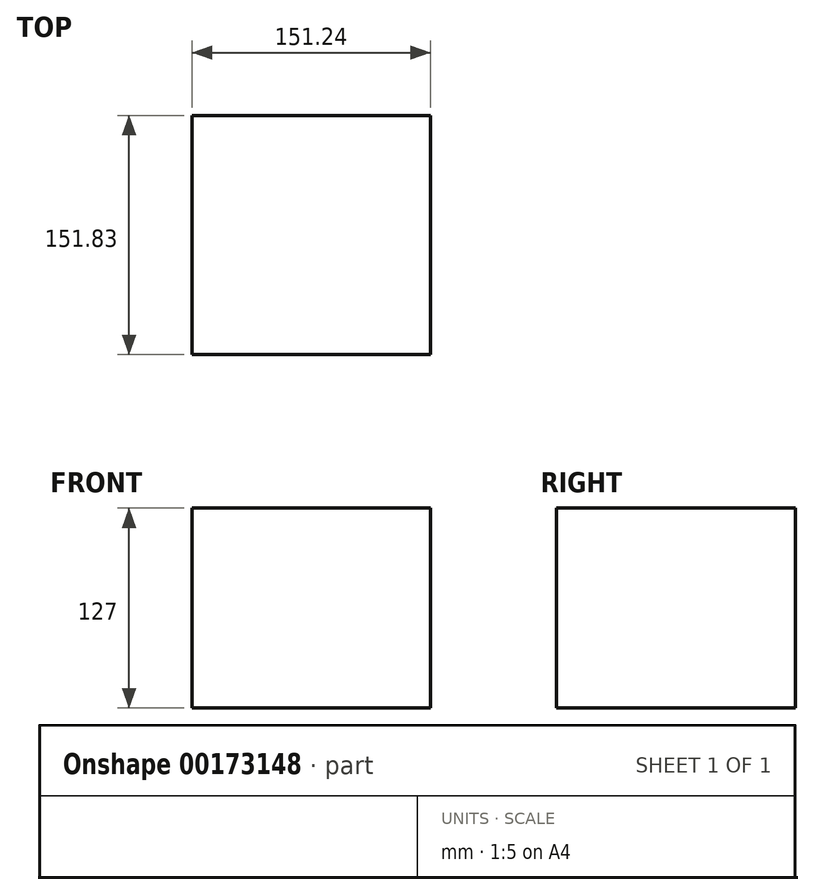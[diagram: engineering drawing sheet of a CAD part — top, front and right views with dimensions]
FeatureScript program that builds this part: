
annotation { "Feature Type Name" : "Feature", "Feature Type Description" : "" }
export const myFeature = defineFeature(function(context is Context, id is Id, definition is map)
    precondition{}
    {
        {
            var Q0;
            Q0=qCreatedBy(makeId("Top.planeOp"),FACE);
            var sketch = newSketch(context, id + "F0", { "sketchPlane" : qUnion([Q0])});
            skLineSegment(sketch, "E0.bottom", {"start": v(-75.62, -75.33) * mm, "end": v(75.62, -75.33) * mm});
            skLineSegment(sketch, "E0.top", {"start": v(-75.62, 76.5) * mm, "end": v(75.62, 76.5) * mm});
            skLineSegment(sketch, "E0.left", {"start": v(-75.62, -75.33) * mm, "end": v(-75.62, 76.5) * mm});
            skLineSegment(sketch, "E0.right", {"start": v(75.62, -75.33) * mm, "end": v(75.62, 76.5) * mm});
            skSolve(sketch);
        }
        {
            var Q0;
            Q0=makeQuery(id+"F0.imprint","IMPRINT",FACE,{"disambiguationData":[TD([[makeQuery(id+"F0.imprint","IMPRINT",EDGE,{"derivedFrom":sQuery(id+"F0.wireOp",EDGE,"E0.bottom")}),1.0]])]});
            extrude(context, id + "F1", {"entities" : qUnion([Q0]), "depth" : 127 * mm});
        }
    });
